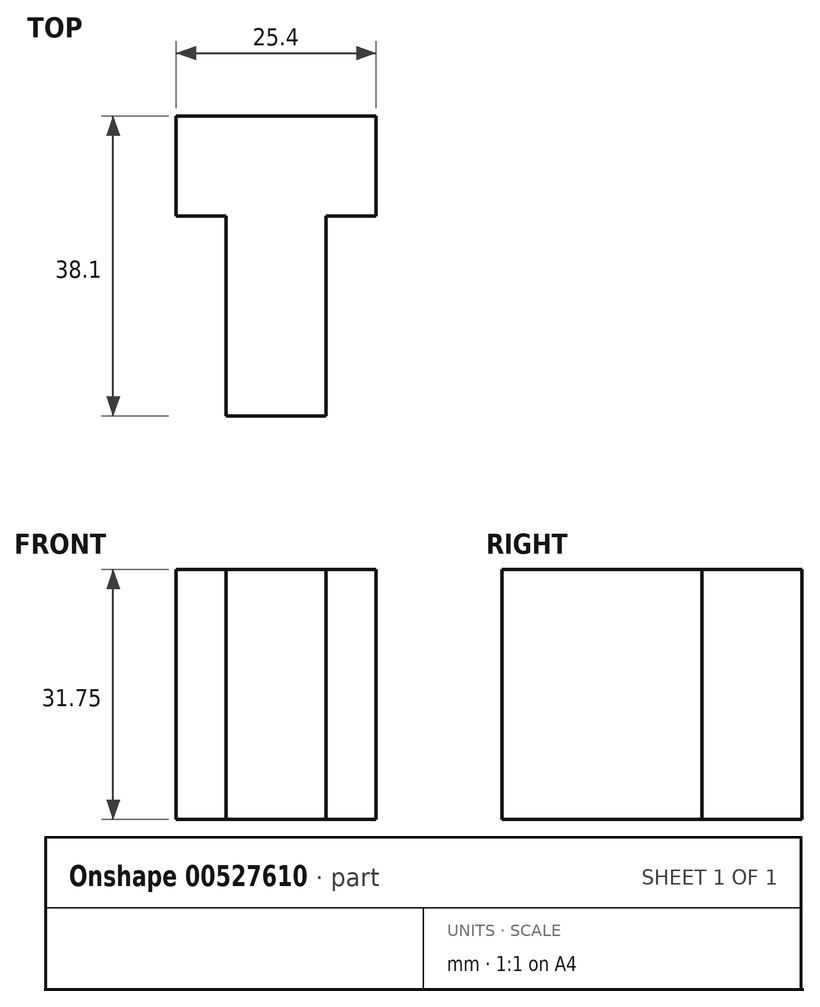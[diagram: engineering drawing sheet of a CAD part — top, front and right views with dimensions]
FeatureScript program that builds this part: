
annotation { "Feature Type Name" : "Feature", "Feature Type Description" : "" }
export const myFeature = defineFeature(function(context is Context, id is Id, definition is map)
    precondition{}
    {
        {
            var Q0;
            Q0=qCreatedBy(makeId("Top.planeOp"),FACE);
            var sketch = newSketch(context, id + "F0", { "sketchPlane" : qUnion([Q0])});
            skLineSegment(sketch, "E0.bottom", {"start": v(-5.57, 30.85) * mm, "end": v(19.83, 30.85) * mm});
            skLineSegment(sketch, "E0.top", {"start": v(-5.57, -7.25) * mm, "end": v(19.83, -7.25) * mm});
            skLineSegment(sketch, "E0.left", {"start": v(-5.57, 30.85) * mm, "end": v(-5.57, -7.25) * mm});
            skLineSegment(sketch, "E0.right", {"start": v(19.83, 30.85) * mm, "end": v(19.83, -7.25) * mm});
            skSolve(sketch);
        }
        {
            var Q0;
            Q0 = qSketchRegion(id + "F0", true);
            extrude(context, id + "F1", {"entities" : qUnion([Q0]), "depth" : 31.75 * mm, "offsetDistance" : 25.4 * mm});
        }
        {
            var Q0;
            Q0=makeQuery(id+"F1.opExtrude","CAP_FACE",FACE,{"disambiguationData":[OSD([sQuery(id+"F0.wireOp",EDGE,"E0.bottom"),sQuery(id+"F0.wireOp",EDGE,"E0.top"),sQuery(id+"F0.wireOp",EDGE,"E0.left"),sQuery(id+"F0.wireOp",EDGE,"E0.right")])],"isStart":false});
            var sketch = newSketch(context, id + "F2", { "sketchPlane" : qUnion([Q0])});
            skLineSegment(sketch, "E1", {"start": v(-5.57, 30.85) * mm, "end": v(-5.57, 18.15) * mm});
            skLineSegment(sketch, "E2", {"start": v(-5.57, 18.15) * mm, "end": v(0.78, 18.15) * mm});
            skLineSegment(sketch, "E3", {"start": v(0.78, 18.15) * mm, "end": v(0.78, -7.25) * mm});
            skLineSegment(sketch, "E4", {"start": v(0.78, -7.25) * mm, "end": v(13.48, -7.25) * mm});
            skLineSegment(sketch, "E5", {"start": v(13.48, -7.25) * mm, "end": v(13.48, 18.15) * mm});
            skLineSegment(sketch, "E6", {"start": v(13.48, 18.15) * mm, "end": v(19.83, 18.15) * mm});
            skLineSegment(sketch, "E7", {"start": v(19.83, 18.15) * mm, "end": v(19.83, 30.85) * mm});
            skLineSegment(sketch, "E8", {"start": v(19.83, 30.85) * mm, "end": v(-5.57, 30.85) * mm});
            skSolve(sketch);
        }
        {
            var Q0;
            {var subQ0=sQuery(id+"F2.wireOp",EDGE,"E2");Q0=makeQuery(id+"F2.imprint","IMPRINT",FACE,{"disambiguationData":[TD([[makeQuery(id+"F2.imprint","IMPRINT",EDGE,{"derivedFrom":subQ0}),-1.0]])]});}
            var Q1;
            {var subQ0=sQuery(id+"F2.wireOp",EDGE,"E5");Q1=makeQuery(id+"F2.imprint","IMPRINT",FACE,{"disambiguationData":[TD([[makeQuery(id+"F2.imprint","IMPRINT",EDGE,{"derivedFrom":subQ0}),-1.0]])]});}
            extrude(context, id + "F3", {"entities" : qUnion([Q0, Q1]), "operationType" : NewBodyOperationType.REMOVE, "oppositeDirection" : true, "depth" : 254 * mm, "offsetDistance" : 25.4 * mm});
        }
    });
